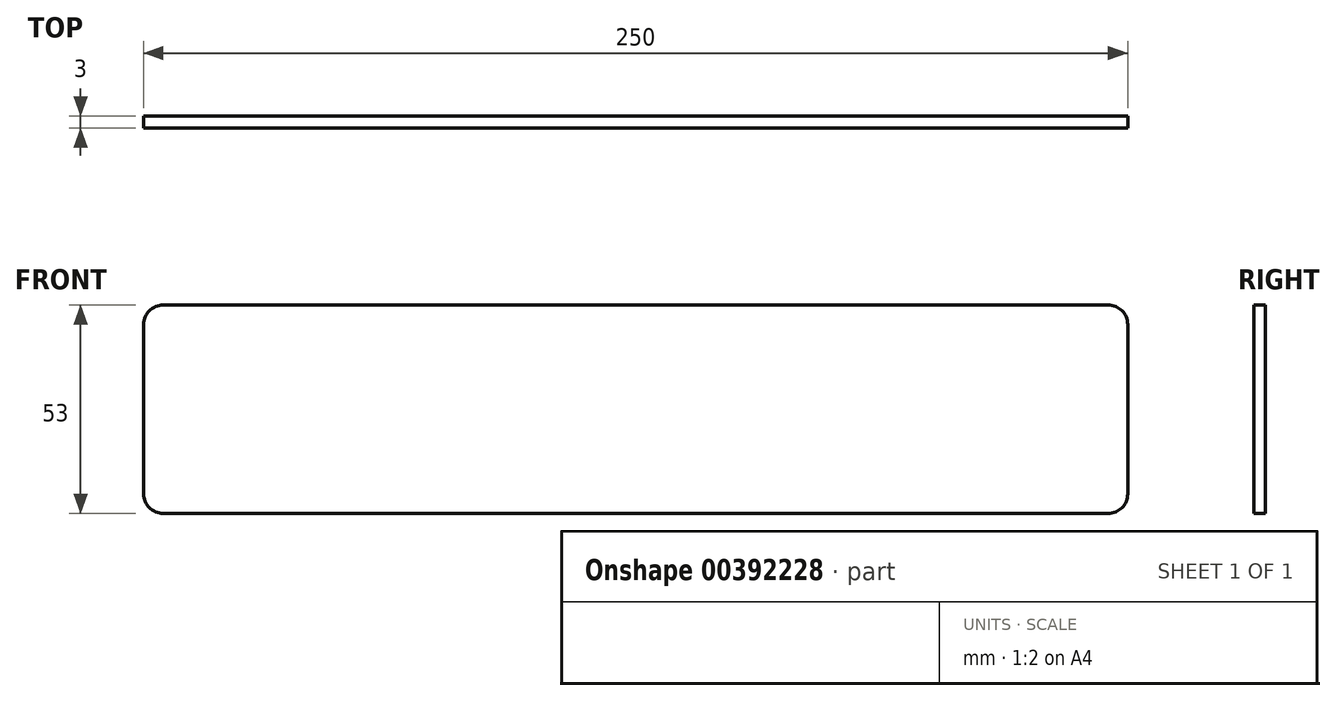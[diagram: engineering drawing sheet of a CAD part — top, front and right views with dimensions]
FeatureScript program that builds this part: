
annotation { "Feature Type Name" : "Feature", "Feature Type Description" : "" }
export const myFeature = defineFeature(function(context is Context, id is Id, definition is map)
    precondition{}
    {
        {
            var Q0;
            Q0=qCreatedBy(makeId("Front.planeOp"),FACE);
            var sketch = newSketch(context, id + "F0", { "sketchPlane" : qUnion([Q0])});
            skLineSegment(sketch, "E0.bottom", {"start": v(5, 0) * mm, "end": v(245, 0) * mm});
            skLineSegment(sketch, "E0.top", {"start": v(5, 53) * mm, "end": v(245, 53) * mm});
            skLineSegment(sketch, "E0.left", {"start": v(0, 5) * mm, "end": v(0, 48) * mm});
            skLineSegment(sketch, "E0.right", {"start": v(250, 5) * mm, "end": v(250, 48) * mm});
            skPoint(sketch, "E1.visualSharp", {"position": v(0, 53) * mm});
            skArc(sketch, "E1.filletArc", {"start": v(5, 53) * mm, "mid": v(1.46, 51.54) * mm, "end": v(0, 48) * mm});
            skPoint(sketch, "E2.visualSharp", {"position": v(0, 0) * mm});
            skArc(sketch, "E2.filletArc", {"start": v(0, 5) * mm, "mid": v(1.46, 1.46) * mm, "end": v(5, 0) * mm});
            skPoint(sketch, "E3.visualSharp", {"position": v(250, 0) * mm});
            skArc(sketch, "E3.filletArc", {"start": v(245, 0) * mm, "mid": v(248.54, 1.46) * mm, "end": v(250, 5) * mm});
            skPoint(sketch, "E4.visualSharp", {"position": v(250, 53) * mm});
            skArc(sketch, "E4.filletArc", {"start": v(250, 48) * mm, "mid": v(248.54, 51.54) * mm, "end": v(245, 53) * mm});
            skSolve(sketch);
        }
        {
            var Q0;
            Q0 = qSketchRegion(id + "F0", true);
            extrude(context, id + "F1", {"entities" : qUnion([Q0]), "depth" : 3 * mm});
        }
    });
